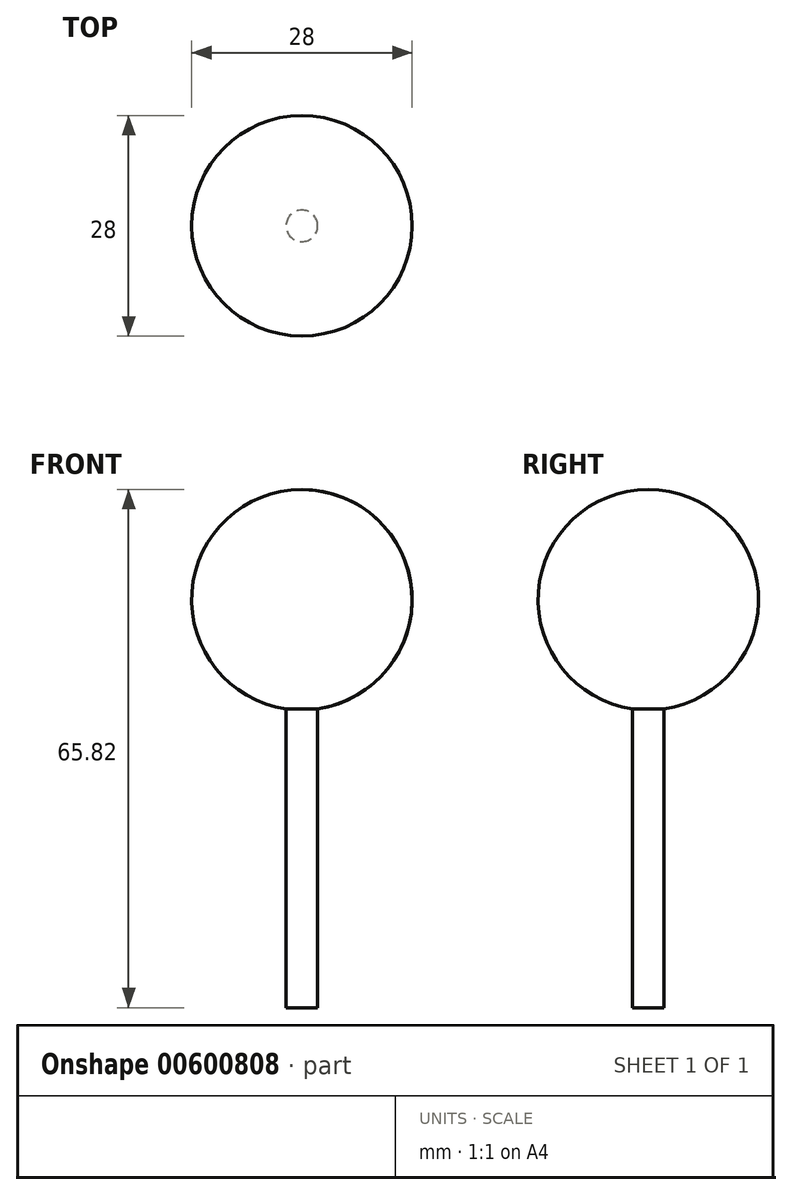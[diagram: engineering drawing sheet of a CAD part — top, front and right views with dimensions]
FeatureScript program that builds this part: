
annotation { "Feature Type Name" : "Feature", "Feature Type Description" : "" }
export const myFeature = defineFeature(function(context is Context, id is Id, definition is map)
    precondition{}
    {
        {
            var Q0;
            Q0=qCreatedBy(makeId("Front.planeOp"),FACE);
            var sketch = newSketch(context, id + "F0", { "sketchPlane" : qUnion([Q0])});
            skArc(sketch, "E0", {"start": v(2, -13.86) * mm, "mid": v(13.96, 1) * mm, "end": v(0, 14) * mm});
            skPoint(sketch, "E1", {"position": v(2, -51.82) * mm});
            skLineSegment(sketch, "E2", {"start": v(0, -51.82) * mm, "end": v(2, -51.82) * mm});
            skLineSegment(sketch, "E3", {"start": v(2, -51.82) * mm, "end": v(2, -13.86) * mm});
            skLineSegment(sketch, "E4", {"start": v(0, 30.34) * mm, "end": v(0, -61.14) * mm, "construction": true});
            skPoint(sketch, "E4.endSnap0", {"position": v(0, 14) * mm});
            skLineSegment(sketch, "E5", {"start": v(0, 14) * mm, "end": v(0, -51.82) * mm});
            skSolve(sketch);
        }
        {
            var Q0;
            Q0=makeQuery(id+"F0.imprint","IMPRINT",FACE,{"disambiguationData":[TD([[makeQuery(id+"F0.imprint","IMPRINT",EDGE,{"derivedFrom":sQuery(id+"F0.wireOp",EDGE,"E0")}),1.0]])]});
            var Q1;
            Q1=sQuery(id+"F0.wireOp",EDGE,"E4");
            revolve(context, id + "F1", {"entities" : qUnion([Q0]), "axis" : qUnion([Q1]), "revolveType" : RevolveType.FULL});
        }
    });
